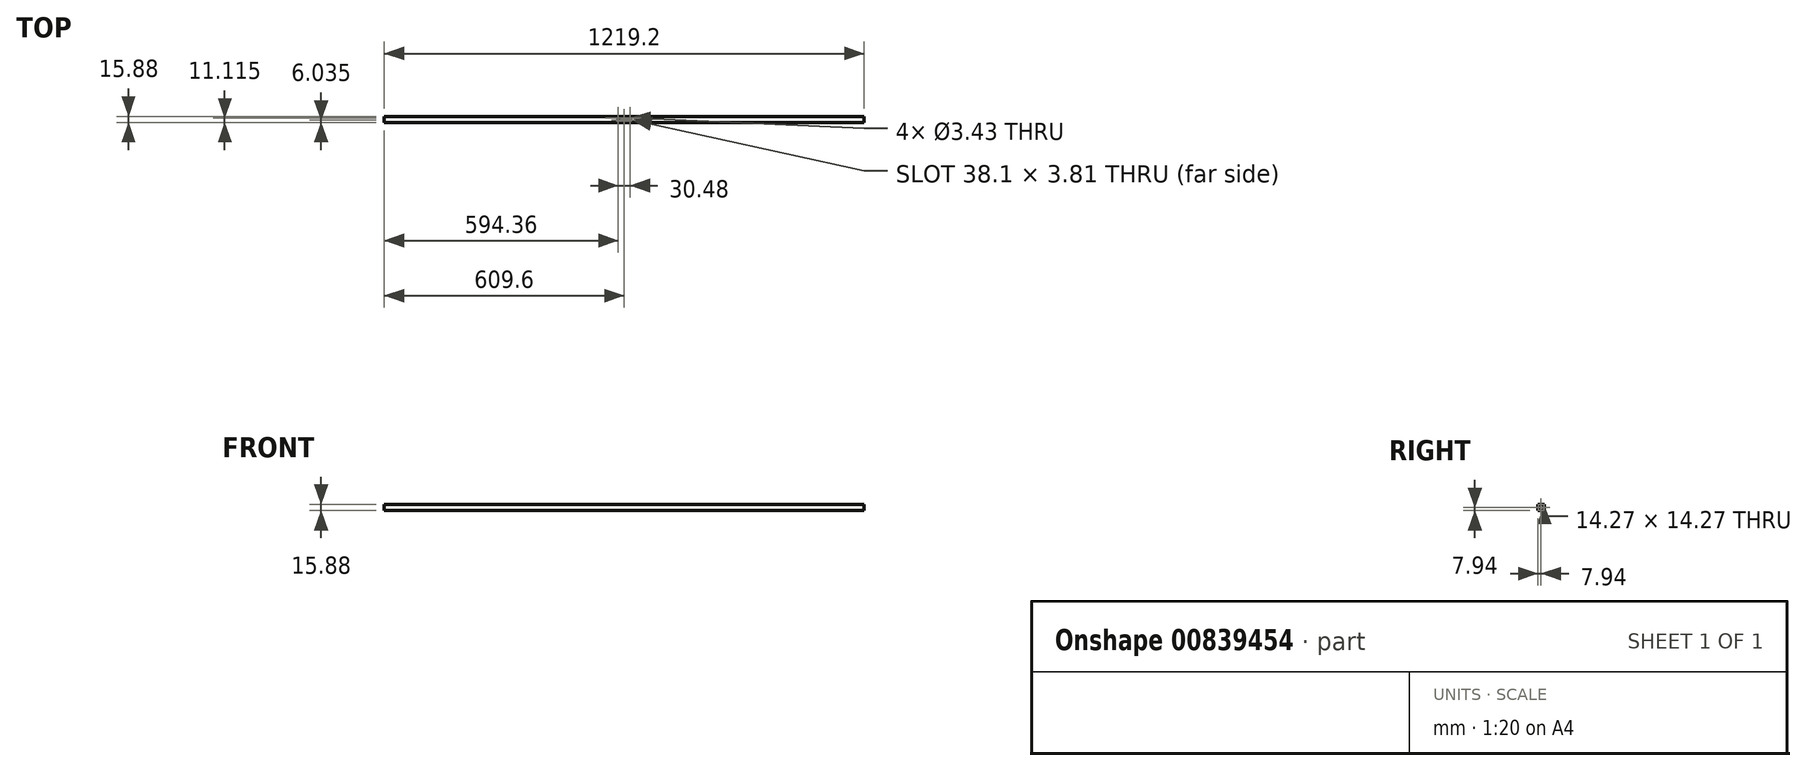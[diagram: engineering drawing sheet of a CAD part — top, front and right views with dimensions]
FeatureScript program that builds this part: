
annotation { "Feature Type Name" : "Feature", "Feature Type Description" : "" }
export const myFeature = defineFeature(function(context is Context, id is Id, definition is map)
    precondition{}
    {
        {
            var Q0;
            Q0=qCreatedBy(makeId("Right.planeOp"),FACE);
            var sketch = newSketch(context, id + "F0", { "sketchPlane" : qUnion([Q0])});
            skLineSegment(sketch, "E0.bottom", {"start": v(-7.94, -7.94) * mm, "end": v(7.94, -7.94) * mm});
            skLineSegment(sketch, "E0.top", {"start": v(-7.94, 7.94) * mm, "end": v(7.94, 7.94) * mm});
            skLineSegment(sketch, "E0.left", {"start": v(-7.94, -7.94) * mm, "end": v(-7.94, 7.94) * mm});
            skLineSegment(sketch, "E0.right", {"start": v(7.94, -7.94) * mm, "end": v(7.94, 7.94) * mm});
            skPoint(sketch, "E0.middle", {"position": v(0, 0) * mm});
            skLineSegment(sketch, "E1.bottom", {"start": v(-7.14, -7.14) * mm, "end": v(7.14, -7.14) * mm});
            skLineSegment(sketch, "E1.top", {"start": v(-7.14, 7.14) * mm, "end": v(7.14, 7.14) * mm});
            skLineSegment(sketch, "E1.left", {"start": v(-7.14, -7.14) * mm, "end": v(-7.14, 7.14) * mm});
            skLineSegment(sketch, "E1.right", {"start": v(7.14, -7.14) * mm, "end": v(7.14, 7.14) * mm});
            skSolve(sketch);
        }
        {
            var Q0;
            Q0 = qSketchRegion(id + "F0", true);
            extrude(context, id + "F1", {"entities" : qUnion([Q0]), "depth" : 1219.2 * mm, "offsetDistance" : 25.4 * mm, "symmetric" : true});
        }
        {
            var Q0;
            Q0=makeQuery(id+"F1.opExtrude","SWEPT_FACE",FACE,{"disambiguationData":[OSD([sQuery(id+"F0.wireOp",EDGE,"E0.bottom")])]});
            var sketch = newSketch(context, id + "F2", { "sketchPlane" : qUnion([Q0])});
            skLineSegment(sketch, "E2", {"start": v(0, 0) * mm, "end": v(17.14, 0) * mm, "construction": true});
            skLineSegment(sketch, "E3.bottom", {"start": v(19.05, 0) * mm, "end": v(-17.14, 0) * mm});
            skLineSegment(sketch, "E3.top", {"start": v(17.14, 3.81) * mm, "end": v(-17.14, 3.8) * mm});
            skLineSegment(sketch, "E3.left", {"start": v(19.05, 1.9) * mm, "end": v(19.05, 1.9) * mm});
            skLineSegment(sketch, "E3.right", {"start": v(-19.05, 1.9) * mm, "end": v(-19.05, 1.9) * mm});
            skPoint(sketch, "E4.visualSharp", {"position": v(-19.05, 3.8) * mm});
            skArc(sketch, "E4.filletArc", {"start": v(-17.14, 3.8) * mm, "mid": v(-18.5, 3.25) * mm, "end": v(-19.05, 1.9) * mm});
            skPoint(sketch, "E5.visualSharp", {"position": v(-19.05, 0) * mm});
            skArc(sketch, "E5.filletArc", {"start": v(-19.05, 1.9) * mm, "mid": v(-18.5, 0.56) * mm, "end": v(-17.14, 0) * mm});
            skPoint(sketch, "E6.visualSharp", {"position": v(19.05, 0) * mm});
            skArc(sketch, "E6.filletArc", {"start": v(17.14, 0) * mm, "mid": v(18.5, 0.56) * mm, "end": v(19.05, 1.9) * mm});
            skPoint(sketch, "E7.visualSharp", {"position": v(19.05, 3.81) * mm});
            skArc(sketch, "E7.filletArc", {"start": v(19.05, 1.9) * mm, "mid": v(18.5, 3.25) * mm, "end": v(17.14, 3.8) * mm});
            skSolve(sketch);
        }
        {
            var Q0;
            Q0 = qSketchRegion(id + "F2", true);
            extrude(context, id + "F3", {"entities" : qUnion([Q0]), "operationType" : NewBodyOperationType.REMOVE, "oppositeDirection" : true, "depth" : 5.08 * mm, "offsetDistance" : 25.4 * mm});
        }
        {
            var Q0;
            Q0=makeQuery(id+"F1.opExtrude","SWEPT_FACE",FACE,{"disambiguationData":[OSD([sQuery(id+"F0.wireOp",EDGE,"E0.bottom")])]});
            var sketch = newSketch(context, id + "F4", { "sketchPlane" : qUnion([Q0])});
            skLineSegment(sketch, "E8", {"start": v(0, 0) * mm, "end": v(0, -3.18) * mm, "construction": true});
            skLineSegment(sketch, "E9", {"start": v(0, -3.18) * mm, "end": v(-15.24, -3.18) * mm, "construction": true});
            skLineSegment(sketch, "E10", {"start": v(0, -3.18) * mm, "end": v(15.24, -3.18) * mm, "construction": true});
            skCircle(sketch, "E11", {"center": v(-15.24, -3.18) * mm, "radius": 1.71 * mm});
            skCircle(sketch, "E12", {"center": v(15.24, -3.18) * mm, "radius": 1.71 * mm});
            skSolve(sketch);
        }
        {
            var Q0;
            Q0 = qSketchRegion(id + "F4", true);
            extrude(context, id + "F5", {"entities" : qUnion([Q0]), "operationType" : NewBodyOperationType.REMOVE, "endBound" : BoundingType.THROUGH_ALL, "oppositeDirection" : true, "depth" : 25.4 * mm, "offsetDistance" : 25.4 * mm});
        }
    });
